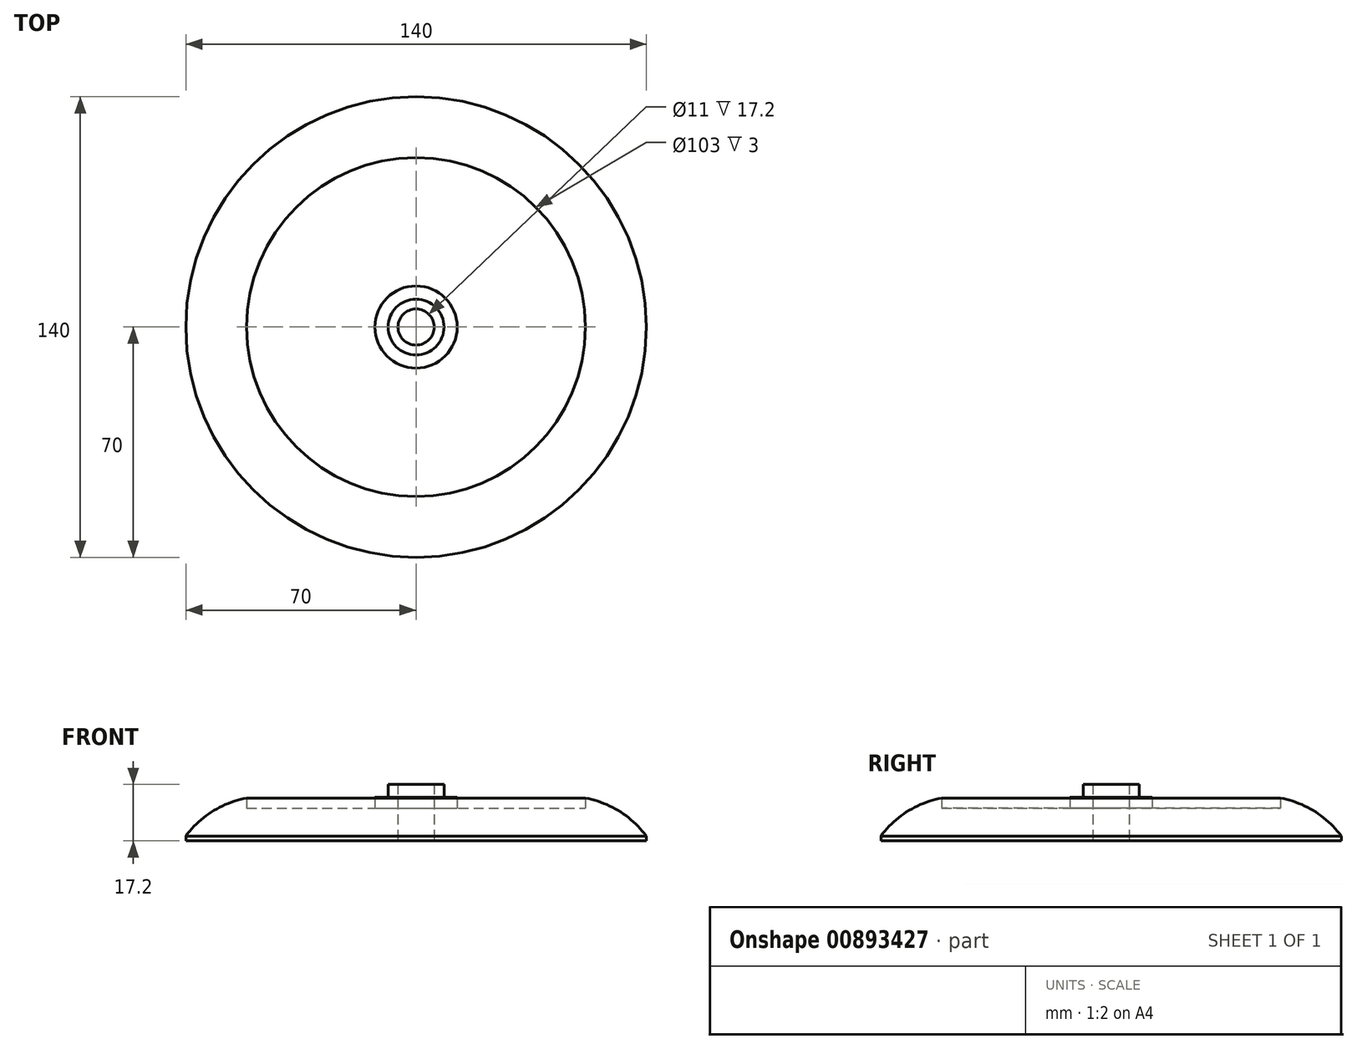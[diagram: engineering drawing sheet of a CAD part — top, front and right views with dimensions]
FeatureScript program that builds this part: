
annotation { "Feature Type Name" : "Feature", "Feature Type Description" : "" }
export const myFeature = defineFeature(function(context is Context, id is Id, definition is map)
    precondition{}
    {
        {
            var Q0;
            Q0=qCreatedBy(makeId("Front.planeOp"),FACE);
            var sketch = newSketch(context, id + "F0", { "sketchPlane" : qUnion([Q0])});
            skLineSegment(sketch, "E0", {"start": v(0, 0) * mm, "end": v(0, 21.92) * mm});
            skLineSegment(sketch, "E1", {"start": v(-70, 0) * mm, "end": v(-5.5, 0) * mm});
            skLineSegment(sketch, "E2", {"start": v(-5.5, 0) * mm, "end": v(-5.5, 17.2) * mm});
            skLineSegment(sketch, "E3", {"start": v(-5.5, 17.2) * mm, "end": v(-8.5, 17.2) * mm});
            skLineSegment(sketch, "E4", {"start": v(-8.5, 17.2) * mm, "end": v(-8.5, 13.2) * mm});
            skLineSegment(sketch, "E5", {"start": v(-8.5, 13.2) * mm, "end": v(-12.5, 13.2) * mm});
            skLineSegment(sketch, "E6", {"start": v(-12.5, 13.2) * mm, "end": v(-12.5, 10) * mm});
            skLineSegment(sketch, "E7", {"start": v(-12.5, 10) * mm, "end": v(-51.5, 10) * mm});
            skLineSegment(sketch, "E8", {"start": v(-70, 1.5) * mm, "end": v(-70, 0) * mm});
            skLineSegment(sketch, "E9", {"start": v(-51.5, 10) * mm, "end": v(-51.5, 13) * mm});
            skLineSegment(sketch, "E10", {"start": v(-46.25, -16.07) * mm, "end": v(-51.63, -16.07) * mm});
            skArc(sketch, "E11", {"start": v(-51.5, 13) * mm, "mid": v(-61.85, 9.02) * mm, "end": v(-70, 1.5) * mm});
            skPoint(sketch, "E12.orphan", {"position": v(-70, 7.39) * mm});
            skSolve(sketch);
        }
        {
            var Q0;
            Q0=makeQuery(id+"F0.imprint","IMPRINT",FACE,{"disambiguationData":[TD([[makeQuery(id+"F0.imprint","IMPRINT",EDGE,{"derivedFrom":sQuery(id+"F0.wireOp",EDGE,"E1")}),1.0]])]});
            var Q1;
            Q1=sQuery(id+"F0.wireOp",EDGE,"E0");
            revolve(context, id + "F1", {"surfaceOperationType" : NewSurfaceOperationType.NEW, "entities" : qUnion([Q0]), "axis" : qUnion([Q1]), "revolveType" : RevolveType.FULL});
        }
    });
